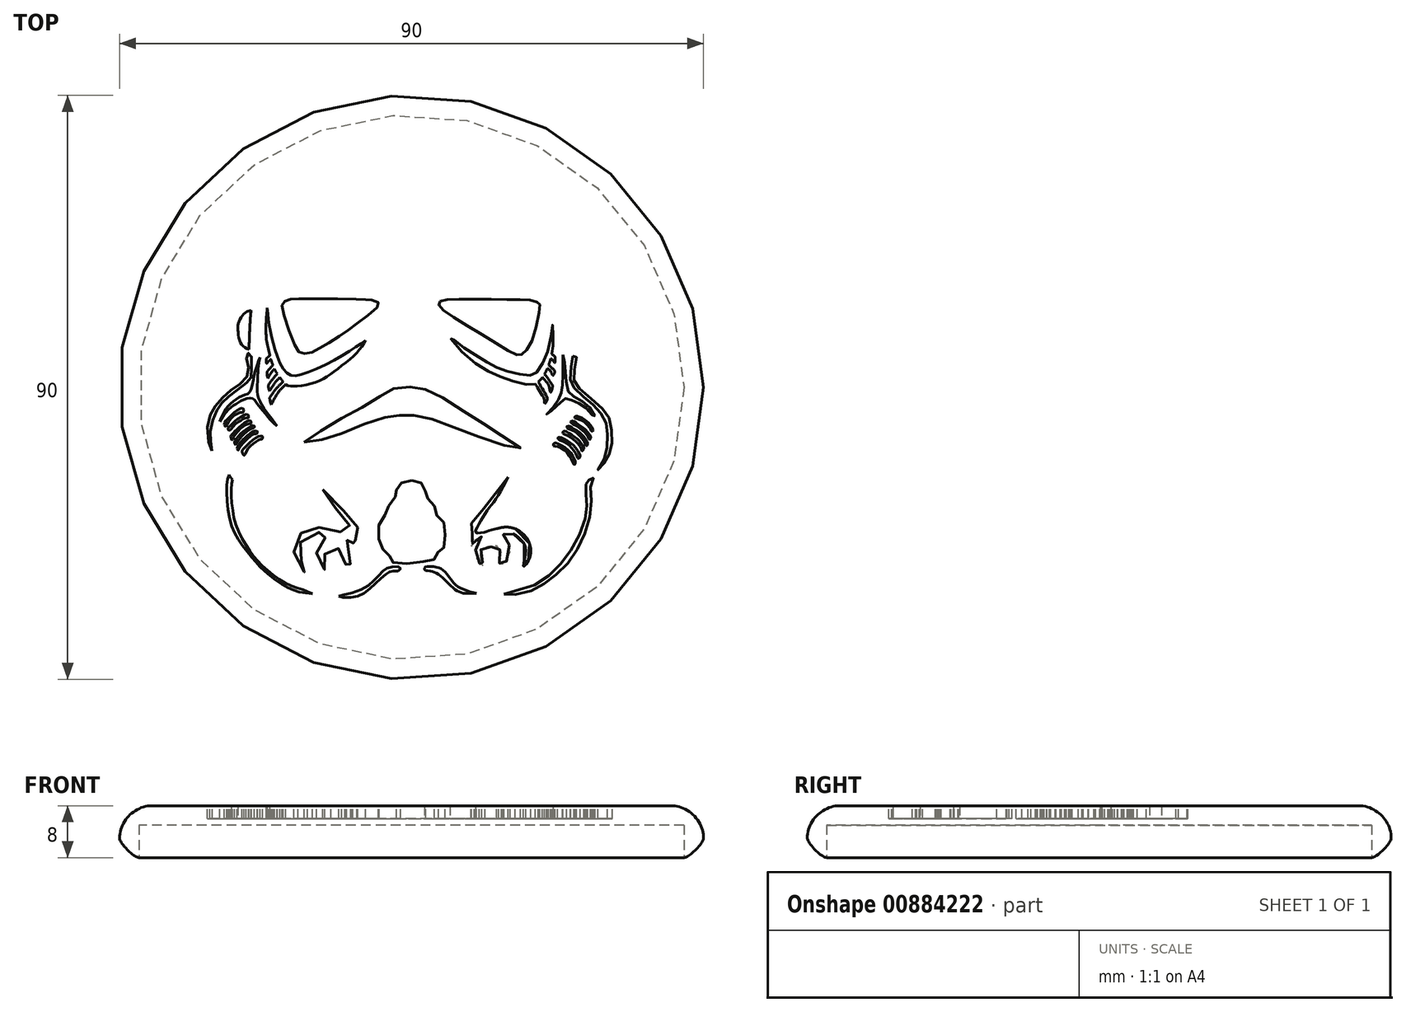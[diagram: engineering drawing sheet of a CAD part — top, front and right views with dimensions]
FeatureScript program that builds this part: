
annotation { "Feature Type Name" : "Feature", "Feature Type Description" : "" }
export const myFeature = defineFeature(function(context is Context, id is Id, definition is map)
    precondition{}
    {
        {
            var Q0;
            Q0=qCreatedBy(makeId("Top.planeOp"),FACE);
            var sketch = newSketch(context, id + "F0", { "sketchPlane" : qUnion([Q0])});
            skCircle(sketch, "E0", {"center": v(0, 0) * mm, "radius": 45 * mm});
            skSolve(sketch);
        }
        {
            var Q0;
            Q0=makeQuery(id+"F0.imprint","IMPRINT",FACE,{"disambiguationData":[TD([[makeQuery(id+"F0.imprint","IMPRINT",EDGE,{"derivedFrom":sQuery(id+"F0.wireOp",EDGE,"E0")}),1.0]])]});
            extrude(context, id + "F1", {"entities" : qUnion([Q0]), "depth" : 8 * mm, "offsetDistance" : 25 * mm});
        }
        {
            var Q0;
            Q0=makeQuery(id+"F1.opExtrude","CAP_EDGE",EDGE,{"disambiguationData":[OSD([sQuery(id+"F0.wireOp",EDGE,"E0")])],"isStart":false});
            fillet(context, id + "F2", {"entities" : qUnion([Q0]), "radius" : 5 * mm, "tangentPropagation" : true, "rho" : 0.4, "crossSection" : FilletCrossSection.CONIC, "allowEdgeOverflow" : false});
        }
        {
            var Q0;
            Q0=makeQuery(id+"F1.opExtrude","CAP_EDGE",EDGE,{"disambiguationData":[OSD([sQuery(id+"F0.wireOp",EDGE,"E0")])],"isStart":true});
            fillet(context, id + "F3", {"entities" : qUnion([Q0]), "radius" : 3 * mm, "rho" : 0.2, "crossSection" : FilletCrossSection.CONIC, "allowEdgeOverflow" : false});
        }
        {
            var Q0;
            Q0=makeQuery(id+"F1.opExtrude","CAP_FACE",FACE,{"disambiguationData":[OSD([sQuery(id+"F0.wireOp",EDGE,"E0")])],"isStart":false});
            var sketch = newSketch(context, id + "F4", { "sketchPlane" : qUnion([Q0])});
            skFitSpline(sketch, "E1", {"points": [v(-21.1, 18.56) * mm, v(-20.45, 25.65) * mm, v(-13.67, 34.04) * mm, v(-6.3, 35.9) * mm], "startDerivative": vector(-0.11, 19.47) * mm, "endDerivative": vector(17.4, 3) * mm});
            skArc(sketch, "E2", {"start": v(-6.3, 35.9) * mm, "mid": v(-6.16, 36.08) * mm, "end": v(-6.3, 36.25) * mm});
            skFitSpline(sketch, "E3", {"points": [v(-6.3, 36.25) * mm, v(-13.36, 34.86) * mm, v(-20.35, 27.7) * mm, v(-22.04, 18.33) * mm], "startDerivative": vector(-18.42, -0.82) * mm, "endDerivative": vector(-1.95, -31.23) * mm});
            skFitSpline(sketch, "E4", {"points": [v(-21.1, 18.56) * mm, v(-4.35, 18.56) * mm, v(8.22, 18.26) * mm, v(21.17, 18.18) * mm], "startDerivative": vector(33.6, 1.82) * mm, "endDerivative": vector(30.75, -1.1) * mm});
            skFitSpline(sketch, "E5", {"points": [v(21.17, 18.18) * mm, v(20.51, 25.57) * mm, v(17.96, 30.6) * mm, v(12.45, 34.48) * mm, v(6.64, 35.9) * mm], "startDerivative": vector(1.5, 28.07) * mm, "endDerivative": vector(-25.84, 4.14) * mm});
            skArc(sketch, "E6", {"start": v(6.64, 36.29) * mm, "mid": v(6.46, 36.1) * mm, "end": v(6.64, 35.9) * mm});
            skLineSegment(sketch, "E7", {"start": v(-22.04, 18.33) * mm, "end": v(-23.47, 18.25) * mm});
            skFitSpline(sketch, "E8", {"points": [v(-23.47, 18.25) * mm, v(-24, 16.99) * mm, v(-24, 14.18) * mm, v(-24, 14.15) * mm], "startDerivative": vector(-1.67, -2.34) * mm, "endDerivative": vector(-0.02, -0.24) * mm});
            skLineSegment(sketch, "E9", {"start": v(-24, 14.16) * mm, "end": v(-23.5, 14.16) * mm});
            skFitSpline(sketch, "E10", {"points": [v(-23.5, 14.16) * mm, v(-23.68, 12.09) * mm, v(-23.43, 9.3) * mm], "startDerivative": vector(-0.53, -4.3) * mm, "endDerivative": vector(0.9, -5.48) * mm});
            skFitSpline(sketch, "E11", {"points": [v(-23.43, 9.3) * mm, v(-23.22, 11.44) * mm, v(-22.82, 13.43) * mm, v(-22.57, 14.26) * mm, v(-22.55, 14.26) * mm], "startDerivative": vector(0.95, 5.81) * mm, "endDerivative": vector(0.55, -0.23) * mm});
            skFitSpline(sketch, "E12", {"points": [v(-22.55, 14.26) * mm, v(-16.3, 14.81) * mm, v(-8.03, 14.6) * mm, v(3.43, 14.26) * mm, v(13.53, 14.32) * mm, v(22.4, 13.88) * mm, v(22.43, 13.88) * mm], "startDerivative": vector(36.91, 4.36) * mm, "endDerivative": vector(1.4, 0.1) * mm});
            skFitSpline(sketch, "E13", {"points": [v(22.43, 13.88) * mm, v(22.6, 11.7) * mm, v(23.06, 8.56) * mm], "startDerivative": vector(0.25, -4.6) * mm, "endDerivative": vector(1, -6) * mm});
            skFitSpline(sketch, "E14", {"points": [v(23.06, 8.56) * mm, v(23.23, 11.4) * mm, v(23.2, 13.79) * mm], "startDerivative": vector(0.42, 5.56) * mm, "endDerivative": vector(-0.14, 4.88) * mm});
            skLineSegment(sketch, "E15", {"start": v(23.2, 13.79) * mm, "end": v(24.07, 13.73) * mm});
            skFitSpline(sketch, "E16", {"points": [v(24.07, 13.73) * mm, v(24.02, 15.62) * mm, v(23.86, 17.16) * mm, v(23.71, 18.04) * mm], "startDerivative": vector(0.2, 5.2) * mm, "endDerivative": vector(-0.16, 0.54) * mm});
            skLineSegment(sketch, "E17", {"start": v(23.71, 18.04) * mm, "end": v(21.97, 18.13) * mm});
            skFitSpline(sketch, "E18", {"points": [v(6.64, 36.29) * mm, v(10.93, 35.62) * mm, v(14.78, 34.1) * mm, v(17.8, 31.84) * mm, v(20.47, 27.99) * mm, v(21.89, 23) * mm, v(21.97, 18.13) * mm], "startDerivative": vector(26.28, -3.05) * mm, "endDerivative": vector(-0.95, -27.87) * mm});
            skFitSpline(sketch, "E19", {"points": [v(24.87, 11.08) * mm, v(24.9, 8.4) * mm, v(25.1, 5.61) * mm, v(25.1, 5.58) * mm], "startDerivative": vector(-0.1, -5.02) * mm, "endDerivative": vector(-0.03, -0.32) * mm});
            skFitSpline(sketch, "E20", {"points": [v(24.87, 11.08) * mm, v(26.19, 10.71) * mm, v(26.76, 9.74) * mm, v(26.76, 6.82) * mm, v(25.99, 5.84) * mm, v(25.1, 5.59) * mm], "startDerivative": vector(7.63, -1.28) * mm, "endDerivative": vector(-5.72, -1.02) * mm});
            skFitSpline(sketch, "E21", {"points": [v(4.4, 13.27) * mm, v(4.17, 12.75) * mm, v(5.67, 11.36) * mm, v(12.79, 6.93) * mm, v(16.43, 4.99) * mm, v(17.14, 5.16) * mm, v(18.6, 7.3) * mm, v(19.77, 12.55) * mm, v(19.7, 12.9) * mm, v(18.75, 13.33) * mm, v(15.14, 13.55) * mm, v(7.27, 13.56) * mm, v(4.4, 13.27) * mm]});
            skFitSpline(sketch, "E22", {"points": [v(-17.36, 13.64) * mm, v(-7.94, 13.58) * mm, v(-6.6, 13.5) * mm, v(-5.22, 13.18) * mm, v(-5.07, 12.6) * mm, v(-8.08, 10.09) * mm, v(-10.86, 8.05) * mm, v(-14.1, 6.08) * mm, v(-15.73, 5.3) * mm, v(-17.05, 5.3) * mm, v(-17.82, 6.1) * mm, v(-19.85, 11.83) * mm, v(-19.82, 13.04) * mm, v(-18.96, 13.5) * mm, v(-17.36, 13.64) * mm]});
            skFitSpline(sketch, "E23", {"points": [v(-24.74, 11.84) * mm, v(-24.93, 9.05) * mm, v(-25.05, 5.84) * mm, v(-25.05, 5.82) * mm], "startDerivative": vector(-0.43, -5.18) * mm, "endDerivative": vector(0, -0.29) * mm});
            skFitSpline(sketch, "E24", {"points": [v(-25.05, 5.84) * mm, v(-26.21, 6.62) * mm, v(-26.72, 8.35) * mm, v(-26.72, 9.82) * mm, v(-26.11, 11) * mm, v(-25.3, 11.7) * mm, v(-24.74, 11.84) * mm], "startDerivative": vector(-7.45, 3.27) * mm, "endDerivative": vector(4.75, 0.67) * mm});
            skFitSpline(sketch, "E25", {"points": [v(-16.55, -8.44) * mm, v(-14.12, -6.82) * mm, v(-10.15, -4.43) * mm, v(-6.62, -2.56) * mm, v(-4.07, -0.9) * mm, v(-2.55, -0.17) * mm, v(-0.37, 0.09) * mm, v(1.49, -0.12) * mm, v(3.44, -0.83) * mm, v(7.04, -3.07) * mm, v(10.93, -5.5) * mm, v(14, -7.52) * mm, v(16.8, -9.43) * mm, v(14.45, -8.98) * mm, v(9.1, -7.16) * mm, v(4.36, -5.38) * mm, v(1.49, -4.44) * mm, v(-0.78, -4.28) * mm, v(-2.04, -4.36) * mm, v(-3.66, -4.57) * mm, v(-6.86, -5.46) * mm, v(-11.08, -7.24) * mm, v(-14.31, -8.2) * mm, v(-16.55, -8.44) * mm]});
            skFitSpline(sketch, "E26", {"points": [v(-6.6, -21.65) * mm, v(-5.95, -20.35) * mm, v(-5.34, -17.76) * mm, v(-4.25, -14.97) * mm, v(-2.1, -13.02) * mm, v(0, -12.58) * mm, v(2.2, -13.3) * mm, v(3.45, -14.36) * mm, v(5.35, -18.33) * mm, v(6.75, -21.36) * mm], "startDerivative": vector(8.55, 14.17) * mm, "endDerivative": vector(9.06, -9.3) * mm});
            skFitSpline(sketch, "E27", {"points": [v(6.75, -21.36) * mm, v(5.76, -20.03) * mm, v(4.64, -18.04) * mm, v(3.6, -15.95) * mm, v(2.18, -14.4) * mm, v(0.21, -13.72) * mm, v(-1.53, -13.84) * mm, v(-2.83, -14.6) * mm, v(-3.96, -16.57) * mm, v(-4.77, -18.7) * mm, v(-5.39, -20.05) * mm, v(-6.6, -21.65) * mm], "startDerivative": vector(-11.93, 14.9) * mm, "endDerivative": vector(-14.69, -17.8) * mm});
            skFitSpline(sketch, "E28", {"points": [v(-22.24, 12.23) * mm, v(-22.02, 10.29) * mm, v(-21.63, 8.12) * mm, v(-21, 5.74) * mm, v(-19.84, 2.95) * mm, v(-18.66, 1.9) * mm, v(-17.3, 1.9) * mm, v(-13.15, 3.57) * mm, v(-9, 5.95) * mm, v(-7.05, 7.25) * mm], "startDerivative": vector(1.9, -19.79) * mm, "endDerivative": vector(16.58, 11.54) * mm});
            skFitSpline(sketch, "E29", {"points": [v(-7.05, 7.25) * mm, v(-8.52, 5.23) * mm, v(-11.72, 2.6) * mm, v(-14.37, 0.95) * mm, v(-17.75, 0.18) * mm, v(-19.24, 0.36) * mm, v(-20, 1.11) * mm, v(-21.07, 2.72) * mm, v(-21.81, 4.87) * mm, v(-22.4, 7.8) * mm, v(-22.24, 12.23) * mm], "startDerivative": vector(-12.4, -20.47) * mm, "endDerivative": vector(3.1, 35.81) * mm});
            skFitSpline(sketch, "E30", {"points": [v(-19.39, 0.45) * mm, v(-20.52, -0.76) * mm, v(-21.64, -2.65) * mm], "startDerivative": vector(-2.51, -2.4) * mm, "endDerivative": vector(-2, -3.78) * mm});
            skFitSpline(sketch, "E31", {"points": [v(-21.64, -2.65) * mm, v(-21.77, -2.21) * mm, v(-21.85, -1.61) * mm], "startDerivative": vector(-0.47, 0.98) * mm, "endDerivative": vector(0.1, 1.1) * mm});
            skFitSpline(sketch, "E32", {"points": [v(-21.85, -1.61) * mm, v(-20.96, -0.33) * mm, v(-19.8, 0.86) * mm], "startDerivative": vector(1.86, 3.03) * mm, "endDerivative": vector(2.48, 2.3) * mm});
            skFitSpline(sketch, "E33", {"points": [v(-20.32, 1.55) * mm, v(-20.97, 0.79) * mm, v(-21.9, -0.59) * mm], "startDerivative": vector(-1.46, -1.6) * mm, "endDerivative": vector(-1.71, -2.64) * mm});
            skFitSpline(sketch, "E34", {"points": [v(-21.9, -0.59) * mm, v(-22.05, 0) * mm, v(-22.08, 0.32) * mm], "startDerivative": vector(-0.29, 1.09) * mm, "endDerivative": vector(-0.05, 0.7) * mm});
            skFitSpline(sketch, "E35", {"points": [v(-22.08, 0.32) * mm, v(-21.54, 1.1) * mm, v(-20.7, 2.08) * mm], "startDerivative": vector(1.07, 1.67) * mm, "endDerivative": vector(1.7, 1.84) * mm});
            skFitSpline(sketch, "E36", {"points": [v(-21.13, 2.83) * mm, v(-21.63, 2.25) * mm, v(-22.13, 1.37) * mm], "startDerivative": vector(-1.12, -1.15) * mm, "endDerivative": vector(-0.9, -1.76) * mm});
            skFitSpline(sketch, "E37", {"points": [v(-22.13, 1.37) * mm, v(-22.26, 1.87) * mm, v(-22.28, 2.37) * mm], "startDerivative": vector(-0.32, 0.99) * mm, "endDerivative": vector(0.01, 1) * mm});
            skFitSpline(sketch, "E38", {"points": [v(-21.38, 3.42) * mm, v(-21.88, 2.87) * mm, v(-22.28, 2.37) * mm], "startDerivative": vector(-1, -1.08) * mm, "endDerivative": vector(-0.82, -1.03) * mm});
            skFitSpline(sketch, "E39", {"points": [v(-21.66, 4.33) * mm, v(-22, 4.05) * mm, v(-22.34, 3.63) * mm], "startDerivative": vector(-0.7, -0.55) * mm, "endDerivative": vector(-0.65, -0.85) * mm});
            skFitSpline(sketch, "E40", {"points": [v(-22.34, 3.63) * mm, v(-22.4, 4.12) * mm, v(-22.39, 4.43) * mm], "startDerivative": vector(-0.13, 0.93) * mm, "endDerivative": vector(0.04, 0.66) * mm});
            skFitSpline(sketch, "E41", {"points": [v(-22.39, 4.43) * mm, v(-22.14, 4.64) * mm, v(-21.82, 4.88) * mm], "startDerivative": vector(0.5, 0.45) * mm, "endDerivative": vector(0.65, 0.46) * mm});
            skFitSpline(sketch, "E42", {"points": [v(-29.59, -5.3) * mm, v(-28.3, -3.53) * mm, v(-27.21, -2.66) * mm, v(-26.03, -2) * mm, v(-24.67, -1.67) * mm, v(-23.78, -2.53) * mm, v(-22.6, -4.03) * mm, v(-20.73, -6) * mm], "startDerivative": vector(7.67, 11.6) * mm, "endDerivative": vector(12.86, -10.66) * mm});
            skFitSpline(sketch, "E43", {"points": [v(-20.73, -6) * mm, v(-22.21, -4.03) * mm, v(-23.61, -1.56) * mm, v(-23.76, 0.5) * mm, v(-23.67, 2.37) * mm, v(-23.48, 4.08) * mm, v(-23.37, 4.66) * mm], "startDerivative": vector(-7.12, 10.84) * mm, "endDerivative": vector(1.1, 5.27) * mm});
            skFitSpline(sketch, "E44", {"points": [v(-29.59, -5.3) * mm, v(-28.74, -3.53) * mm, v(-27.55, -2.22) * mm, v(-26.08, -1.32) * mm, v(-25.02, -0.8) * mm, v(-24.52, 0.53) * mm, v(-24.12, 2.37) * mm, v(-23.37, 4.66) * mm], "startDerivative": vector(5.03, 12.25) * mm, "endDerivative": vector(4.99, 13.95) * mm});
            skFitSpline(sketch, "E45", {"points": [v(-30.75, -9.77) * mm, v(-30.98, -8.14) * mm, v(-31, -6.52) * mm, v(-30.3, -4.14) * mm, v(-29.59, -2.84) * mm, v(-28.48, -1.66) * mm, v(-26.94, -0.49) * mm, v(-25.26, 0.83) * mm, v(-24.73, 1.45) * mm, v(-24.7, 3) * mm, v(-24.74, 5.04) * mm, v(-25.05, 5.31) * mm, v(-25.38, 5.04) * mm, v(-25.42, 4.19) * mm, v(-25.05, 2.67) * mm, v(-25.67, 1.24) * mm, v(-27.21, 0) * mm, v(-28.92, -1.35) * mm, v(-30.37, -3.08) * mm, v(-31.16, -4.67) * mm, v(-31.34, -8.24) * mm, v(-30.75, -9.77) * mm]});
            skFitSpline(sketch, "E46", {"points": [v(-26.1, -3.2) * mm, v(-25.88, -3.43) * mm, v(-25.9, -3.77) * mm, v(-26.3, -3.87) * mm, v(-26.85, -4.05) * mm, v(-27.96, -5.01) * mm, v(-28.62, -6.03) * mm, v(-28.77, -5.98) * mm, v(-28.84, -5.55) * mm, v(-28.2, -4.7) * mm, v(-27.27, -3.86) * mm, v(-26.1, -3.2) * mm]});
            skFitSpline(sketch, "E47", {"points": [v(-25.36, -4.16) * mm, v(-25.19, -4.32) * mm, v(-25.12, -4.67) * mm, v(-25.47, -4.68) * mm, v(-26.12, -5) * mm, v(-27.28, -5.8) * mm, v(-28.13, -6.67) * mm, v(-28.3, -6.36) * mm, v(-28.18, -6.13) * mm, v(-27.41, -5.44) * mm, v(-27, -5.04) * mm, v(-25.36, -4.16) * mm]});
            skFitSpline(sketch, "E48", {"points": [v(-24.9, -5.1) * mm, v(-24.69, -5.41) * mm, v(-24.83, -5.6) * mm, v(-25.42, -5.74) * mm, v(-26.57, -6.57) * mm, v(-27.58, -7.93) * mm, v(-27.7, -8.13) * mm, v(-27.85, -7.69) * mm, v(-27.78, -7.4) * mm, v(-27.14, -6.67) * mm, v(-26.21, -5.86) * mm, v(-24.9, -5.1) * mm]});
            skFitSpline(sketch, "E49", {"points": [v(-24.42, -5.84) * mm, v(-24.23, -6.03) * mm, v(-24.3, -6.25) * mm, v(-24.65, -6.33) * mm, v(-25.6, -7.01) * mm, v(-26.53, -7.97) * mm, v(-27.12, -8.82) * mm, v(-27.23, -8.76) * mm, v(-27.27, -8.46) * mm, v(-27.18, -8.26) * mm, v(-26.58, -7.36) * mm, v(-25.37, -6.4) * mm, v(-24.42, -5.84) * mm]});
            skFitSpline(sketch, "E50", {"points": [v(-23.95, -6.67) * mm, v(-23.74, -6.85) * mm, v(-23.84, -7.12) * mm, v(-24.19, -7.18) * mm, v(-24.94, -7.64) * mm, v(-25.9, -8.54) * mm, v(-26.64, -9.57) * mm, v(-26.7, -9.74) * mm, v(-26.83, -9.54) * mm, v(-26.86, -9.3) * mm, v(-26.05, -8.16) * mm, v(-25.25, -7.4) * mm, v(-23.95, -6.67) * mm]});
            skFitSpline(sketch, "E51", {"points": [v(-23.23, -7.47) * mm, v(-22.93, -7.66) * mm, v(-23.01, -7.96) * mm, v(-23.1, -8.01) * mm, v(-23.48, -8.09) * mm, v(-24.5, -8.75) * mm, v(-25.4, -9.74) * mm, v(-25.8, -10.5) * mm, v(-25.94, -10.39) * mm, v(-26.11, -10.05) * mm, v(-26.09, -9.73) * mm, v(-25.37, -8.93) * mm, v(-24.19, -7.93) * mm, v(-23.23, -7.47) * mm]});
            skFitSpline(sketch, "E52", {"points": [v(-28.13, -13.45) * mm, v(-27.9, -13.85) * mm, v(-27.62, -14.24) * mm], "startDerivative": vector(0.5, -1) * mm, "endDerivative": vector(0.67, -0.88) * mm});
            skFitSpline(sketch, "E53", {"points": [v(-27.62, -14.24) * mm, v(-27.8, -15.5) * mm, v(-27.62, -18.54) * mm, v(-26.92, -21.61) * mm, v(-25.25, -24.72) * mm, v(-23.71, -26.78) * mm, v(-21.61, -28.71) * mm, v(-18.88, -30.44) * mm, v(-16.78, -31.2) * mm, v(-15.3, -31.81) * mm], "startDerivative": vector(-2.83, -14.2) * mm, "endDerivative": vector(16.1, -7.23) * mm});
            skFitSpline(sketch, "E54", {"points": [v(-28.13, -13.45) * mm, v(-28.46, -14.8) * mm, v(-28.36, -18) * mm, v(-27.66, -21.54) * mm, v(-26.34, -24) * mm, v(-24.56, -26.3) * mm, v(-23.32, -27.67) * mm, v(-21.48, -29.31) * mm, v(-19.27, -30.79) * mm, v(-17.42, -31.5) * mm, v(-15.3, -31.81) * mm], "startDerivative": vector(-5.37, -15.97) * mm, "endDerivative": vector(23.37, -2.37) * mm});
            skFitSpline(sketch, "E55", {"points": [v(-13.68, -15.78) * mm, v(-12.9, -16.95) * mm, v(-11.33, -19.12) * mm, v(-9.91, -20.92) * mm, v(-9.41, -21.53) * mm, v(-9.61, -22.33) * mm, v(-10.91, -22.33) * mm, v(-12.89, -21.78) * mm, v(-14.5, -21.61) * mm, v(-15.82, -21.83) * mm, v(-17.3, -22.7) * mm, v(-18.07, -24.32) * mm, v(-18.08, -25.98) * mm, v(-17.24, -27.65) * mm, v(-16.03, -28.82) * mm, v(-16.57, -27.45) * mm, v(-17.34, -26.01) * mm, v(-17.36, -24.38) * mm, v(-16.46, -23.1) * mm, v(-14.83, -22.36) * mm, v(-12.43, -22.61) * mm, v(-12.98, -22.93) * mm, v(-13.92, -23.87) * mm, v(-14.54, -24.79) * mm, v(-14.5, -26.56) * mm, v(-13.6, -28) * mm, v(-13.4, -28.08) * mm, v(-13.62, -27.57) * mm, v(-13.6, -26.39) * mm, v(-13.05, -25.24) * mm, v(-12.22, -25.26) * mm, v(-11.08, -24.84) * mm, v(-10.12, -26.18) * mm, v(-10.2, -27.4) * mm, v(-10.76, -28.1) * mm, v(-9.78, -27.61) * mm, v(-9.12, -25.8) * mm, v(-10.08, -23.31) * mm, v(-10.24, -22.98) * mm, v(-9.7, -23.12) * mm, v(-8.71, -24.67) * mm, v(-8.53, -24.98) * mm, v(-8.51, -24.01) * mm, v(-9.05, -22.86) * mm, v(-8.74, -22.54) * mm, v(-8.3, -21.45) * mm, v(-9.16, -20.43) * mm, v(-11.51, -17.91) * mm, v(-13.68, -15.78) * mm]});
            skFitSpline(sketch, "E56", {"points": [v(-11.2, -32.22) * mm, v(-9.43, -32.42) * mm, v(-7.16, -31.63) * mm, v(-4.98, -29.69) * mm, v(-3.6, -28.55) * mm, v(-2.89, -28.3) * mm, v(-1.82, -28.24) * mm, v(-1.77, -27.76) * mm, v(-3.12, -27.7) * mm, v(-4.33, -28.25) * mm, v(-5.71, -29.74) * mm, v(-8.52, -31.5) * mm, v(-11.2, -32.22) * mm]});
            skFitSpline(sketch, "E57", {"points": [v(0, -14.36) * mm, v(1.37, -14.67) * mm, v(1.98, -15.46) * mm, v(2.24, -16.62) * mm, v(2.56, -17.18) * mm, v(3.48, -18.15) * mm, v(3.6, -19.28) * mm, v(4.78, -20.58) * mm, v(5.06, -21.23) * mm, v(5.13, -24.03) * mm, v(4.81, -24.94) * mm, v(4.08, -25.4) * mm, v(3.69, -26.33) * mm, v(3.04, -26.7) * mm, v(0.21, -27.09) * mm, v(-2.72, -27.06) * mm, v(-3.32, -26.4) * mm, v(-3.5, -25.7) * mm, v(-4.62, -24.78) * mm, v(-5.04, -23.1) * mm, v(-4.9, -20.77) * mm, v(-3.89, -19.37) * mm, v(-3.46, -18.15) * mm, v(-2.5, -16.83) * mm, v(-2.3, -16.3) * mm, v(-2.2, -15.36) * mm, v(-1.4, -14.65) * mm, v(0, -14.36) * mm]});
            skFitSpline(sketch, "E58", {"points": [v(2.16, -28.27) * mm, v(1.98, -27.98) * mm, v(2.13, -27.68) * mm, v(3.6, -27.68) * mm, v(4.56, -27.96) * mm, v(5.55, -28.92) * mm, v(6.71, -30.4) * mm, v(8.05, -31.16) * mm, v(10.01, -31.74) * mm], "startDerivative": vector(-3.43, 4.13) * mm, "endDerivative": vector(12.68, -2.33) * mm});
            skFitSpline(sketch, "E59", {"points": [v(10.01, -31.74) * mm, v(8.05, -31.74) * mm, v(6.71, -31.16) * mm, v(5.01, -29.58) * mm, v(3.6, -28.5) * mm, v(2.16, -28.27) * mm], "startDerivative": vector(-10.02, -0.45) * mm, "endDerivative": vector(-8.23, 0.46) * mm});
            skFitSpline(sketch, "E60", {"points": [v(14.9, -13.87) * mm, v(12.9, -16.43) * mm, v(11.26, -18.51) * mm, v(9.3, -20.9) * mm, v(9.18, -21.21) * mm, v(9.26, -22.35) * mm, v(9.66, -23.02) * mm, v(9.52, -23.3) * mm, v(9.32, -23.85) * mm, v(9.26, -24.61) * mm, v(9.7, -23.62) * mm, v(10.8, -22.89) * mm, v(10.13, -23.94) * mm, v(9.88, -25.5) * mm, v(10.38, -27.06) * mm, v(11.32, -27.72) * mm, v(10.76, -26.72) * mm, v(10.5, -25.5) * mm, v(11.26, -24.44) * mm, v(12.24, -24.6) * mm, v(13.11, -24.4) * mm, v(13.68, -25.2) * mm, v(13.8, -26.46) * mm, v(13.44, -27.57) * mm, v(14.64, -26.83) * mm, v(15.16, -24.73) * mm, v(14.57, -23.2) * mm, v(14.13, -22.65) * mm, v(14.65, -22.32) * mm, v(16.06, -22.8) * mm, v(17.23, -23.96) * mm, v(17.62, -25.46) * mm, v(17.26, -27.61) * mm, v(18.12, -26.55) * mm, v(18.2, -24.1) * mm, v(16, -21.8) * mm], "startDerivative": vector(-47.59, -60.08) * mm, "endDerivative": vector(-89.05, 41.5) * mm});
            skFitSpline(sketch, "E61", {"points": [v(14.9, -13.87) * mm, v(12.9, -17.36) * mm, v(11.58, -19.09) * mm, v(10.25, -21.3) * mm, v(9.92, -22.38) * mm, v(11.4, -22.29) * mm, v(13.1, -21.8) * mm], "startDerivative": vector(-8.8, -16.44) * mm, "endDerivative": vector(23.83, 5.57) * mm});
            skFitSpline(sketch, "E62", {"points": [v(13.1, -21.8) * mm, v(14.66, -21.54) * mm, v(16, -21.8) * mm], "startDerivative": vector(3.06, 0.76) * mm, "endDerivative": vector(2.7, -0.78) * mm});
            skFitSpline(sketch, "E63", {"points": [v(14.27, -31.9) * mm, v(17.25, -31.78) * mm, v(20.7, -30.06) * mm, v(24.03, -27.21) * mm, v(26.62, -22.74) * mm, v(27.72, -18) * mm, v(27.69, -14.68) * mm, v(28.02, -13.91) * mm, v(27.44, -14.17) * mm, v(27, -14.76) * mm, v(26.88, -14.96) * mm, v(26.91, -16.98) * mm, v(26.95, -19.15) * mm, v(25.45, -23.6) * mm, v(22.44, -27.84) * mm, v(18.2, -30.75) * mm, v(14.27, -31.9) * mm]});
            skFitSpline(sketch, "E64", {"points": [v(24.85, 4.82) * mm, v(25.36, 5.1) * mm, v(25.34, 4.23) * mm, v(25.1, 2.3) * mm, v(25.1, 0.94) * mm, v(25.67, 0) * mm, v(27.78, -1.8) * mm, v(29.73, -3.64) * mm, v(30.57, -4.93) * mm, v(30.89, -7.08) * mm, v(30.84, -9.07) * mm, v(30.39, -10.48) * mm, v(29.9, -11.41) * mm, v(28.73, -12.8) * mm, v(29.38, -11.53) * mm, v(30.03, -10.11) * mm, v(30.15, -7.94) * mm, v(30.12, -6.04) * mm, v(29.67, -4.74) * mm, v(28.54, -3.33) * mm, v(27.4, -2.18) * mm, v(25.72, -0.8) * mm, v(24.73, 0.48) * mm, v(24.5, 1.35) * mm, v(24.65, 3.47) * mm, v(24.85, 4.82) * mm]});
            skFitSpline(sketch, "E65", {"points": [v(23.36, 5.04) * mm, v(23.31, 3.47) * mm, v(23.3, 0.75) * mm, v(23.11, -0.66) * mm, v(22.72, -1.72) * mm, v(21.59, -3.38) * mm, v(20.82, -4.2) * mm, v(22.25, -3.03) * mm, v(23.56, -1.8) * mm, v(23.97, -1.68) * mm, v(25.14, -2.19) * mm, v(26.36, -2.8) * mm, v(27.6, -3.94) * mm, v(28.26, -4.63) * mm, v(27.83, -3.6) * mm, v(26.4, -2.22) * mm, v(24.65, -1.17) * mm, v(24.1, -0.4) * mm, v(23.74, 2.01) * mm, v(23.65, 3.47) * mm, v(23.36, 5.04) * mm]});
            skFitSpline(sketch, "E66", {"points": [v(21.84, -9) * mm, v(21.87, -8.74) * mm, v(22.16, -8.55) * mm, v(22.22, -8.57) * mm, v(23.2, -9.02) * mm, v(24.5, -10.07) * mm, v(25.2, -11.27) * mm, v(25.3, -11.5) * mm, v(25.12, -11.95) * mm, v(24.93, -11.73) * mm, v(24.5, -10.81) * mm, v(23.49, -9.65) * mm, v(22.35, -9.13) * mm, v(21.84, -9) * mm]});
            skFitSpline(sketch, "E67", {"points": [v(22.7, -8.03) * mm, v(22.54, -7.84) * mm, v(22.78, -7.66) * mm, v(23.66, -8.04) * mm, v(24.72, -8.73) * mm, v(25.57, -9.75) * mm, v(25.96, -10.52) * mm, v(25.96, -10.66) * mm, v(25.83, -10.95) * mm, v(25.67, -10.99) * mm, v(25.55, -10.7) * mm, v(24.99, -9.71) * mm, v(24.33, -8.99) * mm, v(23.32, -8.33) * mm, v(22.7, -8.03) * mm]});
            skFitSpline(sketch, "E68", {"points": [v(23.3, -7.1) * mm, v(23.37, -6.81) * mm, v(23.55, -6.71) * mm, v(24.02, -6.92) * mm, v(25.15, -7.62) * mm, v(25.8, -8.2) * mm, v(26.27, -8.83) * mm, v(26.56, -9.3) * mm, v(26.58, -9.43) * mm, v(26.47, -9.65) * mm, v(26.3, -9.82) * mm, v(26.17, -9.53) * mm, v(25.66, -8.67) * mm, v(24.83, -7.96) * mm, v(23.83, -7.31) * mm, v(23.3, -7.1) * mm]});
            skFitSpline(sketch, "E69", {"points": [v(23.96, -6.23) * mm, v(23.95, -6.04) * mm, v(24.2, -5.95) * mm, v(24.44, -6.07) * mm, v(25.15, -6.47) * mm, v(25.83, -6.91) * mm, v(26.56, -7.62) * mm, v(27.09, -8.43) * mm, v(27.12, -8.84) * mm, v(26.97, -9.06) * mm, v(26.86, -8.86) * mm, v(26.53, -8.21) * mm, v(25.6, -7.13) * mm, v(24.71, -6.59) * mm, v(23.96, -6.23) * mm]});
            skFitSpline(sketch, "E70", {"points": [v(24.62, -5.5) * mm, v(24.58, -5.24) * mm, v(24.8, -5.16) * mm, v(25.34, -5.46) * mm, v(26.15, -6) * mm, v(27.02, -6.78) * mm, v(27.6, -7.57) * mm, v(27.63, -7.8) * mm, v(27.45, -8.08) * mm, v(27.28, -7.8) * mm, v(26.8, -7.04) * mm, v(26.2, -6.5) * mm, v(25.42, -5.93) * mm, v(24.62, -5.5) * mm]});
            skFitSpline(sketch, "E71", {"points": [v(25.2, -4.76) * mm, v(25.16, -4.55) * mm, v(25.36, -4.42) * mm, v(25.68, -4.48) * mm, v(26.56, -4.9) * mm, v(27.23, -5.44) * mm, v(27.77, -6.07) * mm, v(27.92, -6.48) * mm, v(27.92, -6.76) * mm, v(27.7, -6.68) * mm, v(27.56, -6.41) * mm, v(27.16, -5.87) * mm, v(26.47, -5.25) * mm, v(25.72, -4.92) * mm, v(25.2, -4.76) * mm]});
            skFitSpline(sketch, "E72", {"points": [v(5.93, 7.73) * mm, v(7.08, 6.84) * mm, v(9.1, 5.49) * mm, v(11.7, 3.86) * mm, v(13.44, 2.9) * mm, v(15.35, 2.31) * mm, v(17.74, 1.84) * mm, v(18.66, 1.88) * mm, v(19.43, 2.45) * mm, v(20.52, 4.4) * mm, v(21.37, 7.18) * mm, v(21.75, 9.6) * mm, v(21.8, 7.53) * mm, v(21.81, 6.26) * mm, v(21.65, 5.1) * mm, v(21.06, 3.26) * mm, v(20.44, 1.93) * mm, v(19.55, 0.84) * mm, v(18.74, 0.42) * mm, v(16.75, 0.63) * mm, v(13.9, 1.53) * mm, v(11.49, 2.68) * mm, v(7.98, 5.24) * mm, v(5.93, 7.73) * mm]});
            skFitSpline(sketch, "E73", {"points": [v(19.1, 0.53) * mm, v(19.63, -0.36) * mm, v(20.29, -1.5) * mm, v(20.46, -1.95) * mm, v(20.57, -2.5) * mm, v(20.9, -1.98) * mm, v(20.88, -1.53) * mm, v(20.3, -0.5) * mm, v(19.55, 0.84) * mm], "startDerivative": vector(3.6, -5.96) * mm, "endDerivative": vector(-4.54, 7.83) * mm});
            skFitSpline(sketch, "E74", {"points": [v(20.19, 1.56) * mm, v(20.85, 0.75) * mm, v(21.24, 0) * mm, v(21.45, -0.8) * mm, v(21.72, 0) * mm, v(21.71, 0.36) * mm, v(21.3, 0.97) * mm, v(20.5, 2.04) * mm], "startDerivative": vector(4.44, -5.29) * mm, "endDerivative": vector(-4.55, 6.2) * mm});
            skFitSpline(sketch, "E75", {"points": [v(20.92, 2.89) * mm, v(21.43, 2.49) * mm, v(21.81, 1.82) * mm, v(21.98, 2.1) * mm, v(22.06, 2.45) * mm, v(21.81, 2.84) * mm, v(21.12, 3.43) * mm], "startDerivative": vector(3.06, -1.45) * mm, "endDerivative": vector(-3.57, 2.85) * mm});
            skFitSpline(sketch, "E76", {"points": [v(21.46, 4.42) * mm, v(21.77, 4.18) * mm, v(22.08, 3.8) * mm, v(22.12, 4.45) * mm, v(22.08, 4.77) * mm, v(21.65, 5.1) * mm], "startDerivative": vector(1.68, -0.85) * mm, "endDerivative": vector(-2.5, 1.64) * mm});
            skSolve(sketch);
        }
        {
            var Q0;
            Q0=makeQuery(id+"F4.imprint","IMPRINT",FACE,{"disambiguationData":[TD([[makeQuery(id+"F4.imprint","IMPRINT",EDGE,{"derivedFrom":sQuery(id+"F4.wireOp",EDGE,"E1")}),1.0]])]});
            var Q1;
            Q1=makeQuery(id+"F4.imprint","IMPRINT",FACE,{"disambiguationData":[TD([[makeQuery(id+"F4.imprint","IMPRINT",EDGE,{"derivedFrom":sQuery(id+"F4.wireOp",EDGE,"E22")}),-1.0]])]});
            var Q2;
            Q2=makeQuery(id+"F4.imprint","IMPRINT",FACE,{"disambiguationData":[TD([[makeQuery(id+"F4.imprint","IMPRINT",EDGE,{"derivedFrom":sQuery(id+"F4.wireOp",EDGE,"E21")}),1.0]])]});
            var Q3;
            {var subQ0=sQuery(id+"F4.wireOp",EDGE,"E24");Q3=makeQuery(id+"F4.imprint","IMPRINT",FACE,{"disambiguationData":[TD([[makeQuery(id+"F4.imprint","IMPRINT",EDGE,{"derivedFrom":subQ0}),-1.0]])]});}
            var Q4;
            {var subQ4=sQuery(id+"F4.wireOp",EDGE,"E28");Q4=makeQuery(id+"F4.imprint","IMPRINT",FACE,{"disambiguationData":[TD([[makeQuery(id+"F4.imprint","IMPRINT",EDGE,{"derivedFrom":subQ4}),-1.0]])]});}
            var Q5;
            {var subQ0=sQuery(id+"F4.wireOp",EDGE,"E36");Q5=makeQuery(id+"F4.imprint","IMPRINT",FACE,{"disambiguationData":[TD([[makeQuery(id+"F4.imprint","IMPRINT",EDGE,{"derivedFrom":subQ0}),-1.0]])]});}
            var Q6;
            {var subQ0=sQuery(id+"F4.wireOp",EDGE,"E33");Q6=makeQuery(id+"F4.imprint","IMPRINT",FACE,{"disambiguationData":[TD([[makeQuery(id+"F4.imprint","IMPRINT",EDGE,{"derivedFrom":subQ0}),-1.0]])]});}
            var Q7;
            {var subQ0=sQuery(id+"F4.wireOp",EDGE,"E30");Q7=makeQuery(id+"F4.imprint","IMPRINT",FACE,{"disambiguationData":[TD([[makeQuery(id+"F4.imprint","IMPRINT",EDGE,{"derivedFrom":subQ0}),-1.0]])]});}
            var Q8;
            {var subQ0=sQuery(id+"F4.wireOp",EDGE,"E39");Q8=makeQuery(id+"F4.imprint","IMPRINT",FACE,{"disambiguationData":[TD([[makeQuery(id+"F4.imprint","IMPRINT",EDGE,{"derivedFrom":subQ0}),-1.0]])]});}
            var Q9;
            Q9=makeQuery(id+"F4.imprint","IMPRINT",FACE,{"disambiguationData":[TD([[makeQuery(id+"F4.imprint","IMPRINT",EDGE,{"derivedFrom":sQuery(id+"F4.wireOp",EDGE,"E42")}),1.0]])]});
            var Q10;
            Q10=makeQuery(id+"F4.imprint","IMPRINT",FACE,{"disambiguationData":[TD([[makeQuery(id+"F4.imprint","IMPRINT",EDGE,{"derivedFrom":sQuery(id+"F4.wireOp",EDGE,"E45")}),1.0]])]});
            var Q11;
            Q11=makeQuery(id+"F4.imprint","IMPRINT",FACE,{"disambiguationData":[TD([[makeQuery(id+"F4.imprint","IMPRINT",EDGE,{"derivedFrom":sQuery(id+"F4.wireOp",EDGE,"E46")}),-1.0]])]});
            var Q12;
            Q12=makeQuery(id+"F4.imprint","IMPRINT",FACE,{"disambiguationData":[TD([[makeQuery(id+"F4.imprint","IMPRINT",EDGE,{"derivedFrom":sQuery(id+"F4.wireOp",EDGE,"E47")}),-1.0]])]});
            var Q13;
            Q13=makeQuery(id+"F4.imprint","IMPRINT",FACE,{"disambiguationData":[TD([[makeQuery(id+"F4.imprint","IMPRINT",EDGE,{"derivedFrom":sQuery(id+"F4.wireOp",EDGE,"E48")}),-1.0]])]});
            var Q14;
            Q14=makeQuery(id+"F4.imprint","IMPRINT",FACE,{"disambiguationData":[TD([[makeQuery(id+"F4.imprint","IMPRINT",EDGE,{"derivedFrom":sQuery(id+"F4.wireOp",EDGE,"E49")}),-1.0]])]});
            var Q15;
            Q15=makeQuery(id+"F4.imprint","IMPRINT",FACE,{"disambiguationData":[TD([[makeQuery(id+"F4.imprint","IMPRINT",EDGE,{"derivedFrom":sQuery(id+"F4.wireOp",EDGE,"E50")}),-1.0]])]});
            var Q16;
            Q16=makeQuery(id+"F4.imprint","IMPRINT",FACE,{"disambiguationData":[TD([[makeQuery(id+"F4.imprint","IMPRINT",EDGE,{"derivedFrom":sQuery(id+"F4.wireOp",EDGE,"E51")}),-1.0]])]});
            var Q17;
            Q17=makeQuery(id+"F4.imprint","IMPRINT",FACE,{"disambiguationData":[TD([[makeQuery(id+"F4.imprint","IMPRINT",EDGE,{"derivedFrom":sQuery(id+"F4.wireOp",EDGE,"E25")}),-1.0]])]});
            var Q18;
            {var subQ0=sQuery(id+"F4.wireOp",EDGE,"E27");var subQ1=sQuery(id+"F4.wireOp",EDGE,"E26");var subQ2=makeQuery(id+"F4.imprint","INTERSECT",VERTEX,{"disambiguationData":[OD(0.0)],"derivedFrom":[subQ1,subQ0]});Q18=makeQuery(id+"F4.imprint","IMPRINT",FACE,{"disambiguationData":[TD([[makeQuery(id+"F4.imprint","IMPRINT",EDGE,{"disambiguationData":[TD([[subQ2,-1.0]])],"derivedFrom":subQ1}),-1.0]])]});}
            var Q19;
            {var subQ0=sQuery(id+"F4.wireOp",EDGE,"E20");Q19=makeQuery(id+"F4.imprint","IMPRINT",FACE,{"disambiguationData":[TD([[makeQuery(id+"F4.imprint","IMPRINT",EDGE,{"derivedFrom":subQ0}),-1.0]])]});}
            var Q20;
            Q20=makeQuery(id+"F4.imprint","IMPRINT",FACE,{"disambiguationData":[TD([[makeQuery(id+"F4.imprint","IMPRINT",EDGE,{"derivedFrom":sQuery(id+"F4.wireOp",EDGE,"E57")}),-1.0]])]});
            var Q21;
            Q21=makeQuery(id+"F4.imprint","IMPRINT",FACE,{"disambiguationData":[TD([[makeQuery(id+"F4.imprint","IMPRINT",EDGE,{"derivedFrom":sQuery(id+"F4.wireOp",EDGE,"E55")}),1.0]])]});
            var Q22;
            Q22=makeQuery(id+"F4.imprint","IMPRINT",FACE,{"disambiguationData":[TD([[makeQuery(id+"F4.imprint","IMPRINT",EDGE,{"derivedFrom":sQuery(id+"F4.wireOp",EDGE,"E56")}),1.0]])]});
            var Q23;
            Q23=makeQuery(id+"F4.imprint","IMPRINT",FACE,{"disambiguationData":[TD([[makeQuery(id+"F4.imprint","IMPRINT",EDGE,{"derivedFrom":sQuery(id+"F4.wireOp",EDGE,"E52")}),-1.0]])]});
            var Q24;
            Q24=makeQuery(id+"F4.imprint","IMPRINT",FACE,{"disambiguationData":[TD([[makeQuery(id+"F4.imprint","IMPRINT",EDGE,{"derivedFrom":sQuery(id+"F4.wireOp",EDGE,"E58")}),-1.0]])]});
            var Q25;
            Q25=makeQuery(id+"F4.imprint","IMPRINT",FACE,{"disambiguationData":[TD([[makeQuery(id+"F4.imprint","IMPRINT",EDGE,{"derivedFrom":sQuery(id+"F4.wireOp",EDGE,"E60")}),1.0]])]});
            var Q26;
            Q26=makeQuery(id+"F4.imprint","IMPRINT",FACE,{"disambiguationData":[TD([[makeQuery(id+"F4.imprint","IMPRINT",EDGE,{"derivedFrom":sQuery(id+"F4.wireOp",EDGE,"E63")}),1.0]])]});
            var Q27;
            Q27=makeQuery(id+"F4.imprint","IMPRINT",FACE,{"disambiguationData":[TD([[makeQuery(id+"F4.imprint","IMPRINT",EDGE,{"derivedFrom":sQuery(id+"F4.wireOp",EDGE,"E66")}),-1.0]])]});
            var Q28;
            Q28=makeQuery(id+"F4.imprint","IMPRINT",FACE,{"disambiguationData":[TD([[makeQuery(id+"F4.imprint","IMPRINT",EDGE,{"derivedFrom":sQuery(id+"F4.wireOp",EDGE,"E67")}),-1.0]])]});
            var Q29;
            Q29=makeQuery(id+"F4.imprint","IMPRINT",FACE,{"disambiguationData":[TD([[makeQuery(id+"F4.imprint","IMPRINT",EDGE,{"derivedFrom":sQuery(id+"F4.wireOp",EDGE,"E68")}),-1.0]])]});
            var Q30;
            Q30=makeQuery(id+"F4.imprint","IMPRINT",FACE,{"disambiguationData":[TD([[makeQuery(id+"F4.imprint","IMPRINT",EDGE,{"derivedFrom":sQuery(id+"F4.wireOp",EDGE,"E69")}),-1.0]])]});
            var Q31;
            Q31=makeQuery(id+"F4.imprint","IMPRINT",FACE,{"disambiguationData":[TD([[makeQuery(id+"F4.imprint","IMPRINT",EDGE,{"derivedFrom":sQuery(id+"F4.wireOp",EDGE,"E70")}),-1.0]])]});
            var Q32;
            Q32=makeQuery(id+"F4.imprint","IMPRINT",FACE,{"disambiguationData":[TD([[makeQuery(id+"F4.imprint","IMPRINT",EDGE,{"derivedFrom":sQuery(id+"F4.wireOp",EDGE,"E71")}),-1.0]])]});
            var Q33;
            Q33=makeQuery(id+"F4.imprint","IMPRINT",FACE,{"disambiguationData":[TD([[makeQuery(id+"F4.imprint","IMPRINT",EDGE,{"derivedFrom":sQuery(id+"F4.wireOp",EDGE,"E64")}),-1.0]])]});
            var Q34;
            Q34=makeQuery(id+"F4.imprint","IMPRINT",FACE,{"disambiguationData":[TD([[makeQuery(id+"F4.imprint","IMPRINT",EDGE,{"derivedFrom":sQuery(id+"F4.wireOp",EDGE,"E65")}),1.0]])]});
            var Q35;
            {var subQ1=sQuery(id+"F4.wireOp",EDGE,"E72");var subQ6=sQuery(id+"F4.wireOp",EDGE,"E76");var subQ7=makeQuery(id+"F4.imprint","INTERSECT",VERTEX,{"disambiguationData":[OD(0.0)],"derivedFrom":[subQ1,subQ6]});Q35=makeQuery(id+"F4.imprint","IMPRINT",FACE,{"disambiguationData":[TD([[makeQuery(id+"F4.imprint","IMPRINT",EDGE,{"disambiguationData":[TD([[subQ7,1.0]])],"derivedFrom":subQ1}),-1.0]])]});}
            var Q36;
            {var subQ0=sQuery(id+"F4.wireOp",EDGE,"E73");Q36=makeQuery(id+"F4.imprint","IMPRINT",FACE,{"disambiguationData":[TD([[makeQuery(id+"F4.imprint","IMPRINT",EDGE,{"derivedFrom":subQ0}),1.0]])]});}
            var Q37;
            {var subQ0=sQuery(id+"F4.wireOp",EDGE,"E75");Q37=makeQuery(id+"F4.imprint","IMPRINT",FACE,{"disambiguationData":[TD([[makeQuery(id+"F4.imprint","IMPRINT",EDGE,{"derivedFrom":subQ0}),1.0]])]});}
            var Q38;
            {var subQ0=sQuery(id+"F4.wireOp",EDGE,"E76");Q38=makeQuery(id+"F4.imprint","IMPRINT",FACE,{"disambiguationData":[TD([[makeQuery(id+"F4.imprint","IMPRINT",EDGE,{"derivedFrom":subQ0}),1.0]])]});}
            var Q39;
            {var subQ0=sQuery(id+"F4.wireOp",EDGE,"E74");Q39=makeQuery(id+"F4.imprint","IMPRINT",FACE,{"disambiguationData":[TD([[makeQuery(id+"F4.imprint","IMPRINT",EDGE,{"derivedFrom":subQ0}),1.0]])]});}
            var Q40;
            Q40=sQuery(id+"F4.wireOp",EDGE,"E4");
            extrude(context, id + "F5", {"entities" : qUnion([Q0, Q1, Q2, Q3, Q4, Q5, Q6, Q7, Q8, Q9, Q10, Q11, Q12, Q13, Q14, Q15, Q16, Q17, Q18, Q19, Q20, Q21, Q22, Q23, Q24, Q25, Q26, Q27, Q28, Q29, Q30, Q31, Q32, Q33, Q34, Q35, Q36, Q37, Q38, Q39]), "operationType" : NewBodyOperationType.REMOVE, "surfaceEntities" : qUnion([Q40]), "oppositeDirection" : true, "depth" : 2 * mm, "offsetDistance" : 25 * mm});
        }
        {
            var Q0;
            Q0=makeQuery(id+"F1.opExtrude","CAP_FACE",FACE,{"disambiguationData":[OSD([sQuery(id+"F0.wireOp",EDGE,"E0")])],"isStart":true});
            extrude(context, id + "F6", {"entities" : qUnion([Q0]), "operationType" : NewBodyOperationType.REMOVE, "oppositeDirection" : true, "depth" : 5 * mm, "offsetDistance" : 25 * mm});
        }
    });
